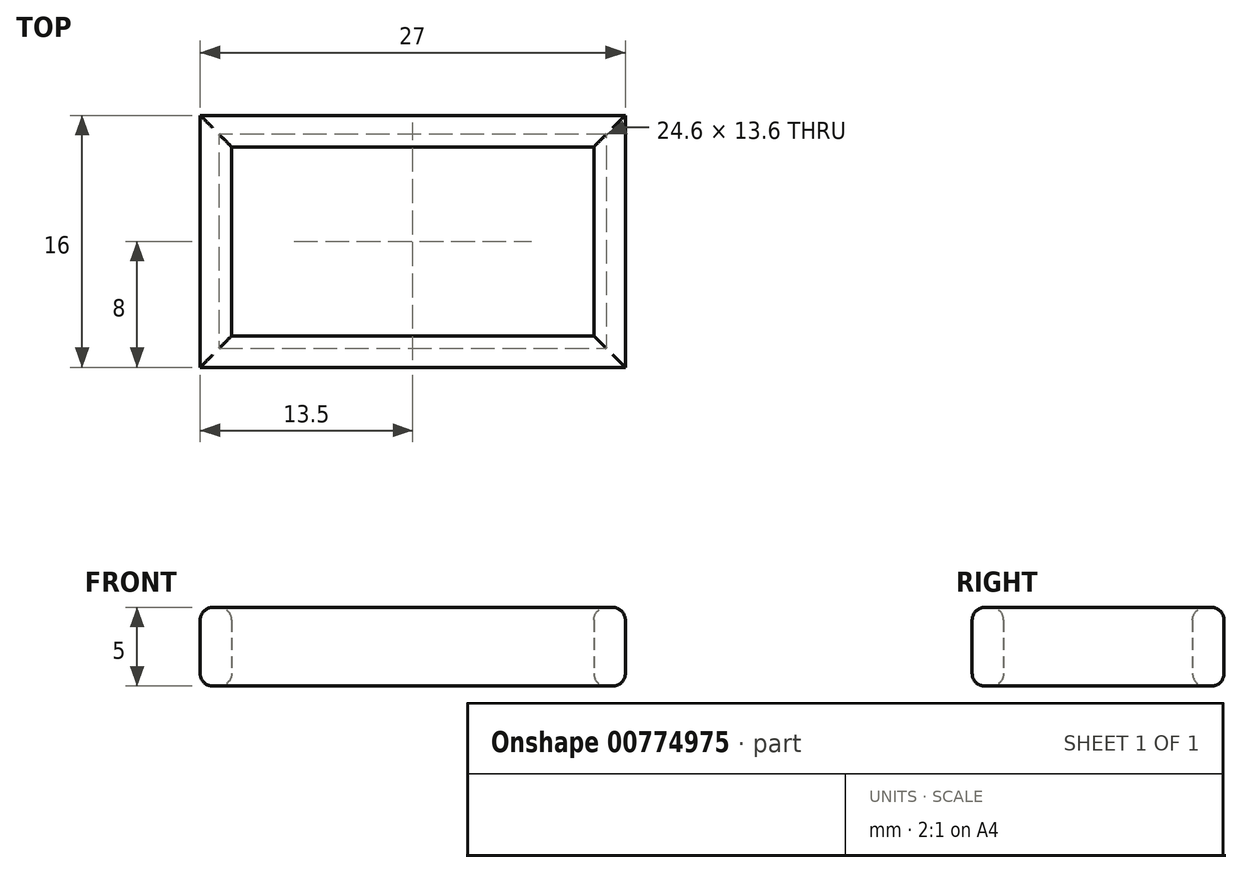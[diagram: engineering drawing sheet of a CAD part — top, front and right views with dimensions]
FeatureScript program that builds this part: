
annotation { "Feature Type Name" : "Feature", "Feature Type Description" : "" }
export const myFeature = defineFeature(function(context is Context, id is Id, definition is map)
    precondition{}
    {
        {
            var Q0;
            Q0=qCreatedBy(makeId("Top.planeOp"),FACE);
            var sketch = newSketch(context, id + "F0", { "sketchPlane" : qUnion([Q0])});
            skLineSegment(sketch, "E0.bottom", {"start": v(11.5, -6) * mm, "end": v(-11.5, -6) * mm});
            skLineSegment(sketch, "E0.top", {"start": v(11.5, 6) * mm, "end": v(-11.5, 6) * mm});
            skLineSegment(sketch, "E0.left", {"start": v(11.5, -6) * mm, "end": v(11.5, 6) * mm});
            skLineSegment(sketch, "E0.right", {"start": v(-11.5, -6) * mm, "end": v(-11.5, 6) * mm});
            skPoint(sketch, "E0.middle", {"position": v(0, 0) * mm});
            skLineSegment(sketch, "E1.0", {"start": v(13.5, 8) * mm, "end": v(-13.5, 8) * mm});
            skLineSegment(sketch, "E1.1", {"start": v(13.5, -8) * mm, "end": v(13.5, 8) * mm});
            skLineSegment(sketch, "E1.2", {"start": v(13.5, -8) * mm, "end": v(-13.5, -8) * mm});
            skLineSegment(sketch, "E1.3", {"start": v(-13.5, -8) * mm, "end": v(-13.5, 8) * mm});
            skSolve(sketch);
        }
        {
            var Q0;
            Q0=makeQuery(id+"F0.imprint","IMPRINT",FACE,{"disambiguationData":[TD([[makeQuery(id+"F0.imprint","IMPRINT",EDGE,{"derivedFrom":sQuery(id+"F0.wireOp",EDGE,"E0.bottom")}),1.0]])]});
            extrude(context, id + "F1", {"entities" : qUnion([Q0]), "depth" : 5 * mm, "offsetDistance" : 25 * mm});
        }
        {
            var Q0;
            Q0=makeQuery(id+"F1.opExtrude","CAP_EDGE",EDGE,{"disambiguationData":[OSD([sQuery(id+"F0.wireOp",EDGE,"E1.0")])],"isStart":false});
            var Q1;
            Q1=makeQuery(id+"F1.opExtrude","CAP_EDGE",EDGE,{"disambiguationData":[OSD([sQuery(id+"F0.wireOp",EDGE,"E1.1")])],"isStart":false});
            var Q2;
            Q2=makeQuery(id+"F1.opExtrude","CAP_EDGE",EDGE,{"disambiguationData":[OSD([sQuery(id+"F0.wireOp",EDGE,"E1.2")])],"isStart":false});
            var Q3;
            Q3=makeQuery(id+"F1.opExtrude","CAP_EDGE",EDGE,{"disambiguationData":[OSD([sQuery(id+"F0.wireOp",EDGE,"E1.3")])],"isStart":false});
            var Q4;
            Q4=makeQuery(id+"F1.opExtrude","CAP_EDGE",EDGE,{"disambiguationData":[OSD([sQuery(id+"F0.wireOp",EDGE,"E0.right")])],"isStart":false});
            var Q5;
            Q5=makeQuery(id+"F1.opExtrude","CAP_EDGE",EDGE,{"disambiguationData":[OSD([sQuery(id+"F0.wireOp",EDGE,"E0.top")])],"isStart":false});
            var Q6;
            Q6=makeQuery(id+"F1.opExtrude","CAP_EDGE",EDGE,{"disambiguationData":[OSD([sQuery(id+"F0.wireOp",EDGE,"E0.bottom")])],"isStart":false});
            var Q7;
            Q7=makeQuery(id+"F1.opExtrude","CAP_EDGE",EDGE,{"disambiguationData":[OSD([sQuery(id+"F0.wireOp",EDGE,"E0.left")])],"isStart":false});
            var Q8;
            Q8=makeQuery(id+"F1.opExtrude","CAP_EDGE",EDGE,{"disambiguationData":[OSD([sQuery(id+"F0.wireOp",EDGE,"E1.2")])],"isStart":true});
            var Q9;
            Q9=makeQuery(id+"F1.opExtrude","CAP_EDGE",EDGE,{"disambiguationData":[OSD([sQuery(id+"F0.wireOp",EDGE,"E0.bottom")])],"isStart":true});
            var Q10;
            Q10=makeQuery(id+"F1.opExtrude","CAP_EDGE",EDGE,{"disambiguationData":[OSD([sQuery(id+"F0.wireOp",EDGE,"E0.top")])],"isStart":true});
            var Q11;
            Q11=makeQuery(id+"F1.opExtrude","CAP_EDGE",EDGE,{"disambiguationData":[OSD([sQuery(id+"F0.wireOp",EDGE,"E1.0")])],"isStart":true});
            var Q12;
            Q12=makeQuery(id+"F1.opExtrude","CAP_EDGE",EDGE,{"disambiguationData":[OSD([sQuery(id+"F0.wireOp",EDGE,"E1.1")])],"isStart":true});
            var Q13;
            Q13=makeQuery(id+"F1.opExtrude","CAP_EDGE",EDGE,{"disambiguationData":[OSD([sQuery(id+"F0.wireOp",EDGE,"E0.left")])],"isStart":true});
            var Q14;
            Q14=makeQuery(id+"F1.opExtrude","CAP_EDGE",EDGE,{"disambiguationData":[OSD([sQuery(id+"F0.wireOp",EDGE,"E1.3")])],"isStart":true});
            var Q15;
            Q15=makeQuery(id+"F1.opExtrude","CAP_EDGE",EDGE,{"disambiguationData":[OSD([sQuery(id+"F0.wireOp",EDGE,"E0.right")])],"isStart":true});
            fillet(context, id + "F2", {"entities" : qUnion([Q0, Q1, Q2, Q3, Q4, Q5, Q6, Q7, Q8, Q9, Q10, Q11, Q12, Q13, Q14, Q15]), "radius" : 0.8 * mm, "tangentPropagation" : true, "allowEdgeOverflow" : false});
        }
    });
